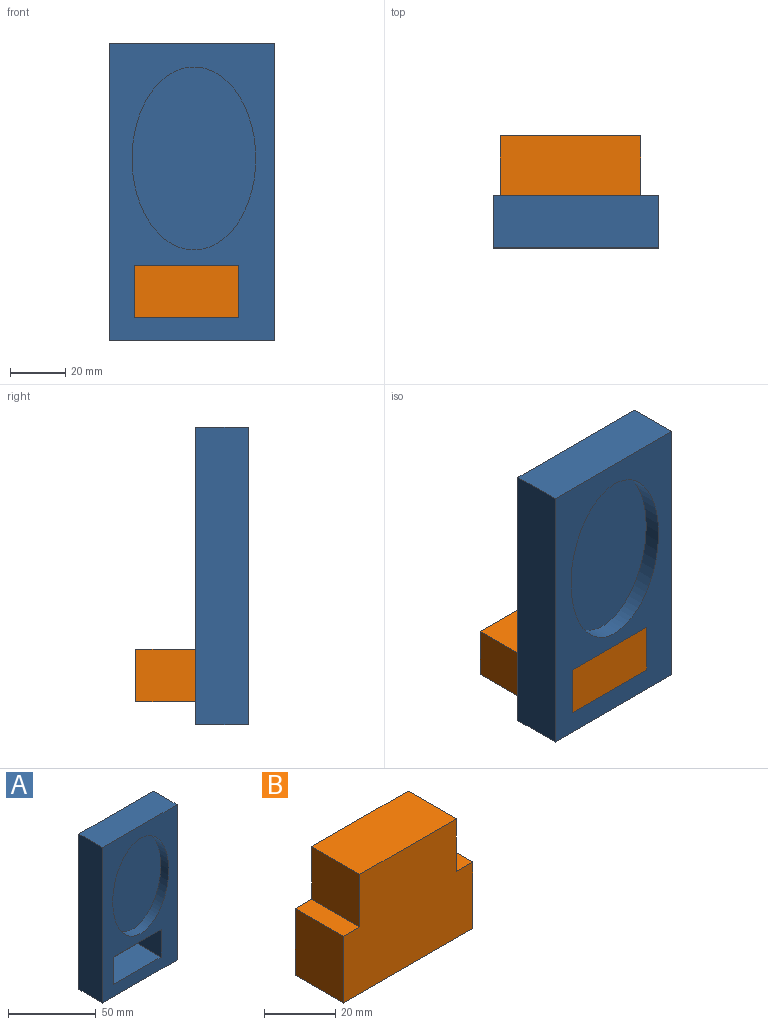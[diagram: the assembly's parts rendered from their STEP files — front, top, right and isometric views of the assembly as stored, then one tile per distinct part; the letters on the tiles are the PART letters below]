
ASSEMBLY  parts=2 mates=1
PART A: 12 faces, bbox 59.9x19.1x108.2 mm
  f0: plane 108.2x59.93mm, normal (0,-1,0), area 3412.1mm2, adj f2,f3,f4,f5,f6,f7,f8,f9
  f1: plane 108.2x59.93mm, normal (0,1,0), area 5758.8mm2, adj f2,f3,f4,f5,f6,f7,f8,f9
  f2: plane 59.93x19.05mm, normal (0,0,1), area 1141.7mm2, adj f0,f1,f3,f5
  f3: plane 108.2x19.05mm, normal (-1,0,0), area 2061.1mm2, adj f0,f1,f2,f4
  f4: plane 59.93x19.05mm, normal (0,0,-1), area 1141.7mm2, adj f0,f1,f3,f5
  f5: plane 108.2x19.05mm, normal (1,0,0), area 2061.1mm2, adj f0,f1,f2,f4
  f6: plane 38.1x19.05mm, normal (0,0,-1), area 725.8mm2, adj f0,f1,f7,f9
  f7: plane 19.05x19.05mm, normal (1,0,0), area 362.9mm2, adj f0,f1,f6,f8
  f8: plane 38.1x19.05mm, normal (0,0,1), area 725.8mm2, adj f0,f1,f7,f9
  f9: plane 19.05x19.05mm, normal (-1,0,0), area 362.9mm2, adj f0,f1,f6,f8
  f10: extruded ~66.45x44.96mm, area 1121.7mm2, adj f0,f11
  f11: plane 66.45x44.96mm, normal (0,-1,0), area 2346.6mm2, adj f10
PART B: 10 faces, bbox 51.1x19.1x40.8 mm
  f0: plane 38.1x19.05mm, normal (0,0,1), area 725.8mm2, adj f1,f7,f8,f9
  f1: plane 19.05x18.03mm, normal (-1,0,0), area 343.4mm2, adj f0,f2,f8,f9
  f2: plane 19.05x6.5mm, normal (0,0,1), area 123.8mm2, adj f1,f3,f8,f9
  f3: plane 22.8x19.05mm, normal (-1,0,0), area 434.4mm2, adj f2,f4,f8,f9
  f4: plane 51.1x19.05mm, normal (0,0,-1), area 973.4mm2, adj f3,f5,f8,f9
  f5: plane 22.8x19.05mm, normal (1,0,0), area 434.4mm2, adj f4,f6,f8,f9
  f6: plane 19.05x6.5mm, normal (0,0,1), area 123.8mm2, adj f5,f7,f8,f9
  f7: plane 19.05x18.03mm, normal (1,0,0), area 343.4mm2, adj f0,f6,f8,f9
  f8: plane 51.1x40.83mm, normal (0,-1,0), area 1852mm2, adj f0,f1,f2,f3,f4,f5,f6,f7
  f9: plane 51.1x40.83mm, normal (0,1,0), area 1852mm2, adj f0,f1,f2,f3,f4,f5,f6,f7
PLACE A t=(75.81,35.12,-14.51)mm
PLACE B rot(axis=(1,0,0),90deg) t=(98.65,41.55,-53.22)mm
MATE fastened B.f0 <-> A.f0  axis (0,-1,0) through (54.05,16.07,-72.27)mm
